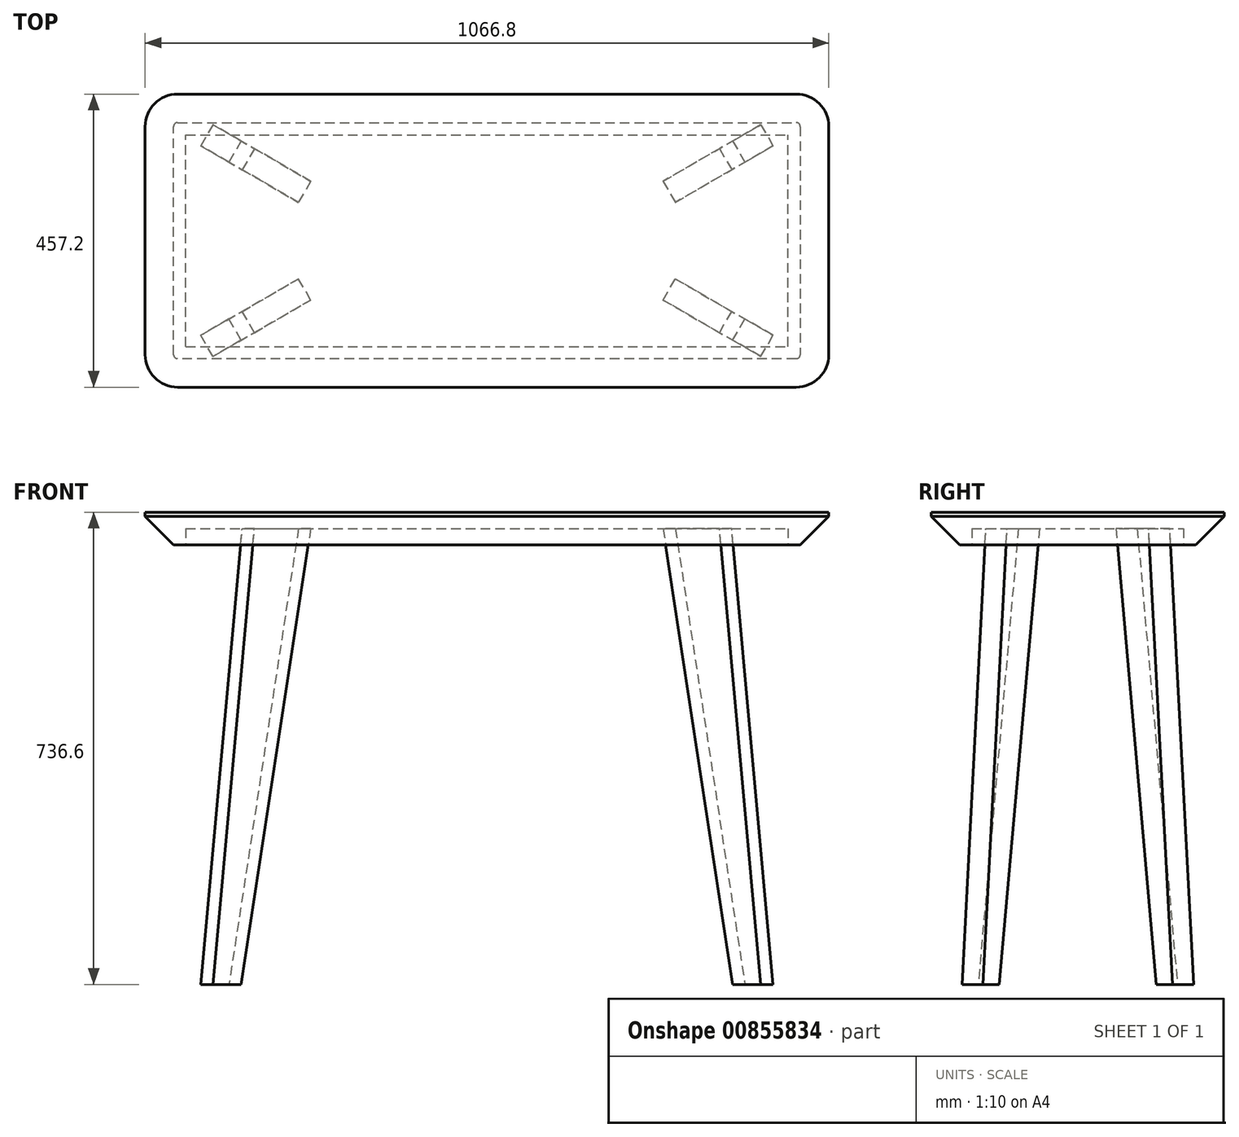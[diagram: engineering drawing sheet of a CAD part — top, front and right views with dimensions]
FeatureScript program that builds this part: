
annotation { "Feature Type Name" : "Feature", "Feature Type Description" : "" }
export const myFeature = defineFeature(function(context is Context, id is Id, definition is map)
    precondition{}
    {
        {
            var Q0;
            Q0=qCreatedBy(makeId("Top.planeOp"),FACE);
            var sketch = newSketch(context, id + "F0", { "sketchPlane" : qUnion([Q0])});
            skLineSegment(sketch, "E0.bottom", {"start": v(-533.4, -228.6) * mm, "end": v(533.4, -228.6) * mm});
            skLineSegment(sketch, "E0.top", {"start": v(-533.4, 228.6) * mm, "end": v(533.4, 228.6) * mm});
            skLineSegment(sketch, "E0.left", {"start": v(-533.4, -228.6) * mm, "end": v(-533.4, 228.6) * mm});
            skLineSegment(sketch, "E0.right", {"start": v(533.4, -228.6) * mm, "end": v(533.4, 228.6) * mm});
            skLineSegment(sketch, "E1", {"start": v(-533.4, 228.6) * mm, "end": v(533.4, -228.6) * mm, "construction": true});
            skLineSegment(sketch, "E2", {"start": v(533.4, 228.6) * mm, "end": v(0, 0) * mm, "construction": true});
            skLineSegment(sketch, "E3", {"start": v(0, 0) * mm, "end": v(-533.4, -228.6) * mm, "construction": true});
            skSolve(sketch);
        }
        {
            var Q0;
            Q0 = qSketchRegion(id + "F0", true);
            extrude(context, id + "F1", {"entities" : qUnion([Q0]), "oppositeDirection" : true, "depth" : 50.8 * mm, "offsetDistance" : 25.4 * mm});
        }
        {
            var Q0;
            Q0=makeQuery(id+"F1.opExtrude","SWEPT_EDGE",EDGE,{"disambiguationData":[OSD([sQuery(id+"F0.wireOp",EDGE,"E0.bottom"),sQuery(id+"F0.wireOp",EDGE,"E0.left")])]});
            var Q1;
            Q1=makeQuery(id+"F1.opExtrude","SWEPT_EDGE",EDGE,{"disambiguationData":[OSD([sQuery(id+"F0.wireOp",EDGE,"E0.top"),sQuery(id+"F0.wireOp",EDGE,"E0.left")])]});
            var Q2;
            Q2=makeQuery(id+"F1.opExtrude","SWEPT_EDGE",EDGE,{"disambiguationData":[OSD([sQuery(id+"F0.wireOp",EDGE,"E0.bottom"),sQuery(id+"F0.wireOp",EDGE,"E0.right")])]});
            var Q3;
            Q3=makeQuery(id+"F1.opExtrude","SWEPT_EDGE",EDGE,{"disambiguationData":[OSD([sQuery(id+"F0.wireOp",EDGE,"E0.top"),sQuery(id+"F0.wireOp",EDGE,"E0.right")])]});
            fillet(context, id + "F2", {"entities" : qUnion([Q0, Q1, Q2, Q3]), "radius" : 50.8 * mm, "tangentPropagation" : true, "allowEdgeOverflow" : false});
        }
        {
            var Q0;
            Q0=makeQuery(id+"F1.opExtrude","CAP_EDGE",EDGE,{"disambiguationData":[OSD([sQuery(id+"F0.wireOp",EDGE,"E0.right")])],"isStart":false});
            chamfer(context, id + "F3", {"entities" : qUnion([Q0]), "width" : 44.45 * mm, "tangentPropagation" : true});
        }
        {
            var Q0;
            Q0=makeQuery(id+"F1.opExtrude","CAP_FACE",FACE,{"disambiguationData":[OSD([sQuery(id+"F0.wireOp",EDGE,"E0.bottom"),sQuery(id+"F0.wireOp",EDGE,"E0.top"),sQuery(id+"F0.wireOp",EDGE,"E0.left"),sQuery(id+"F0.wireOp",EDGE,"E0.right")])],"isStart":false});
            var sketch = newSketch(context, id + "F4", { "sketchPlane" : qUnion([Q0])});
            skLineSegment(sketch, "E4.bottom", {"start": v(-469.9, 165.1) * mm, "end": v(469.9, 165.1) * mm});
            skLineSegment(sketch, "E4.top", {"start": v(-469.9, -165.1) * mm, "end": v(469.9, -165.1) * mm});
            skLineSegment(sketch, "E4.left", {"start": v(-469.9, 165.1) * mm, "end": v(-469.9, -165.1) * mm});
            skLineSegment(sketch, "E4.right", {"start": v(469.9, 165.1) * mm, "end": v(469.9, -165.1) * mm});
            skSolve(sketch);
        }
        {
            var Q0;
            Q0 = qSketchRegion(id + "F4", true);
            extrude(context, id + "F5", {"entities" : qUnion([Q0]), "operationType" : NewBodyOperationType.REMOVE, "oppositeDirection" : true, "depth" : 25.4 * mm, "offsetDistance" : 25.4 * mm});
        }
        {
            var Q0;
            Q0=makeQuery(id+"F1.opExtrude","CAP_FACE",FACE,{"disambiguationData":[OSD([sQuery(id+"F0.wireOp",EDGE,"E0.bottom"),sQuery(id+"F0.wireOp",EDGE,"E0.top"),sQuery(id+"F0.wireOp",EDGE,"E0.left"),sQuery(id+"F0.wireOp",EDGE,"E0.right")])],"isStart":true});
            cPlane(context, id + "F6", {"entities" : qUnion([Q0]), "cplaneType" : CPlaneType.OFFSET, "offset" : 736.6 * mm, "oppositeDirection" : true, "width" : 152.4 * mm, "height" : 152.4 * mm});
        }
        {
            var Q0;
            Q0=makeQuery(id+"F5.boolean.opBoolean","COPY",FACE,{"derivedFrom":makeQuery(id+"F5.opExtrude","CAP_FACE",FACE,{"disambiguationData":[OSD([sQuery(id+"F4.wireOp",EDGE,"E4.bottom"),sQuery(id+"F4.wireOp",EDGE,"E4.top"),sQuery(id+"F4.wireOp",EDGE,"E4.left"),sQuery(id+"F4.wireOp",EDGE,"E4.right")])],"isStart":false})});
            var sketch = newSketch(context, id + "F7", { "sketchPlane" : qUnion([Q0])});
            skLineSegment(sketch, "E5", {"start": v(-152.4, 0) * mm, "end": v(-438.36, 165.1) * mm, "construction": true});
            skSolve(sketch);
        }
        {
            var Q0;
            Q0=sQuery(id+"F7.wireOp",EDGE,"E5");
            cPlane(context, id + "F8", {"entities" : qUnion([Q0]), "cplaneType" : CPlaneType.LINE_ANGLE, "offset" : 25.4 * mm, "angle" : 0 * degree, "width" : 152.4 * mm, "height" : 152.4 * mm});
        }
        {
            var Q0;
            Q0=qCreatedBy(id+"F8.planeOp",FACE);
            var sketch = newSketch(context, id + "F9", { "sketchPlane" : qUnion([Q0])});
            skLineSegment(sketch, "E6", {"start": v(-284.38, -25.4) * mm, "end": v(-409.79, -736.6) * mm});
            skLineSegment(sketch, "E7", {"start": v(-409.79, -736.6) * mm, "end": v(-460.59, -736.6) * mm});
            skLineSegment(sketch, "E8", {"start": v(-460.59, -736.6) * mm, "end": v(-385.98, -25.4) * mm});
            skLineSegment(sketch, "E9", {"start": v(-385.98, -25.4) * mm, "end": v(-284.38, -25.4) * mm});
            skSolve(sketch);
        }
        {
            var Q0;
            Q0 = qSketchRegion(id + "F9", true);
            extrude(context, id + "F10", {"entities" : qUnion([Q0]), "operationType" : NewBodyOperationType.ADD, "endBound" : BoundingType.SYMMETRIC, "depth" : 38.1 * mm, "offsetDistance" : 25.4 * mm});
        }
        {
            var Q0;
            Q0=makeQuery(id+"F1.opExtrude","SWEPT_BODY",BODY,{"disambiguationData":[OSD([sQuery(id+"F0.wireOp",EDGE,"E0.bottom"),sQuery(id+"F0.wireOp",EDGE,"E0.top"),sQuery(id+"F0.wireOp",EDGE,"E0.left"),sQuery(id+"F0.wireOp",EDGE,"E0.right")])]});
            var Q1;
            Q1=qCreatedBy(makeId("Right.planeOp"),FACE);
            mirror(context, id + "F11", {"operationType" : NewBodyOperationType.ADD, "entities" : qUnion([Q0]), "mirrorPlane" : qUnion([Q1])});
        }
        {
            var Q0;
            Q0=makeQuery(id+"F1.opExtrude","SWEPT_BODY",BODY,{"disambiguationData":[OSD([sQuery(id+"F0.wireOp",EDGE,"E0.bottom"),sQuery(id+"F0.wireOp",EDGE,"E0.top"),sQuery(id+"F0.wireOp",EDGE,"E0.left"),sQuery(id+"F0.wireOp",EDGE,"E0.right")])]});
            var Q1;
            Q1=qCreatedBy(makeId("Front.planeOp"),FACE);
            mirror(context, id + "F12", {"operationType" : NewBodyOperationType.ADD, "entities" : qUnion([Q0]), "mirrorPlane" : qUnion([Q1])});
        }
    });
